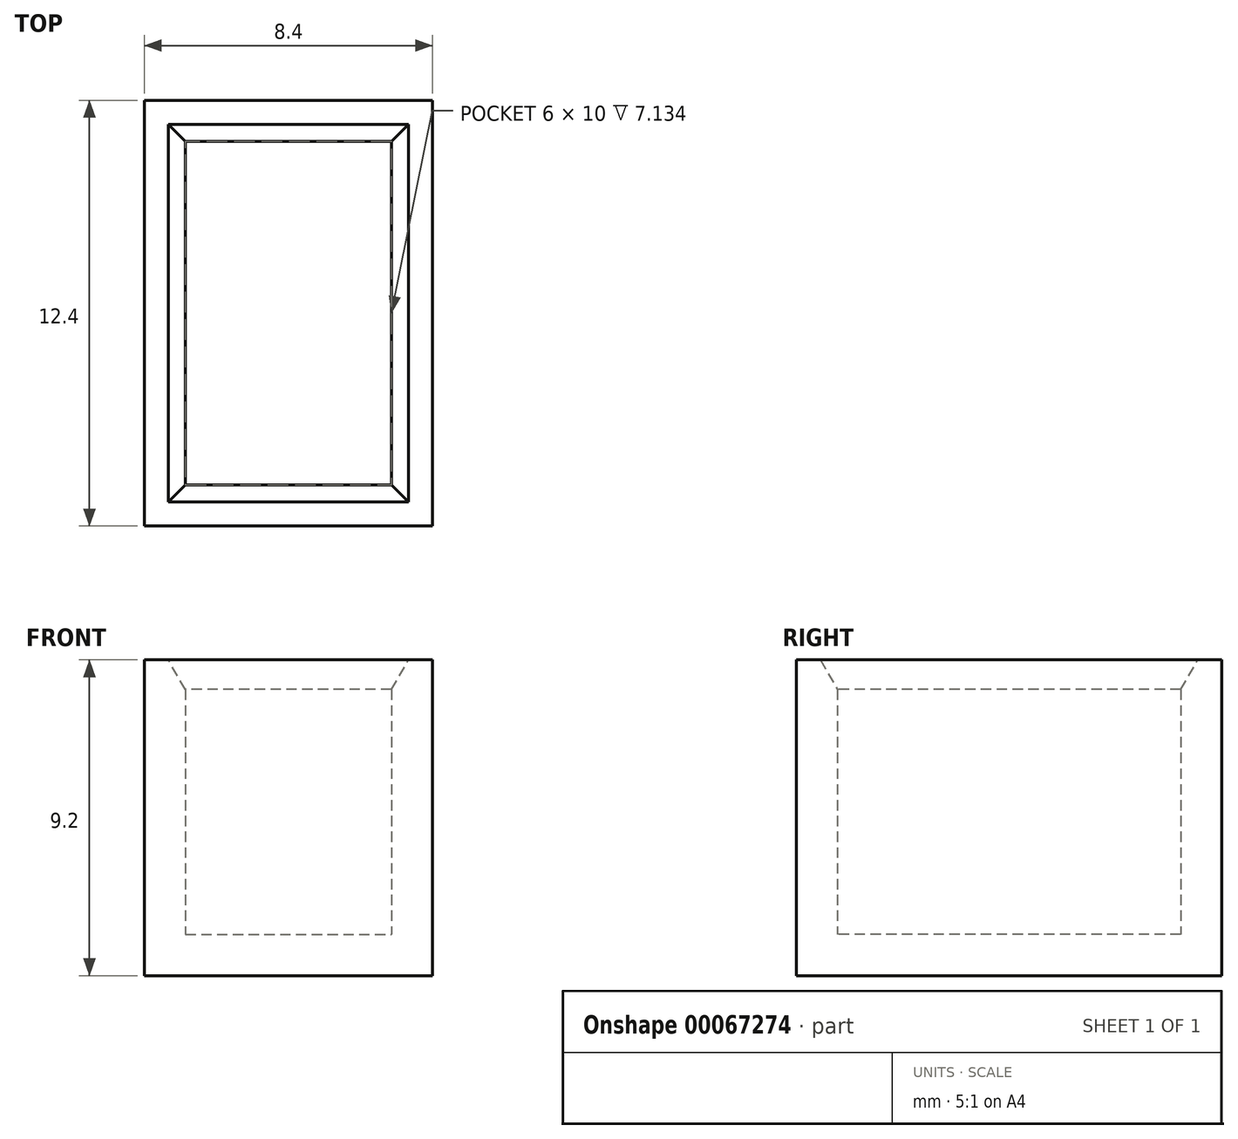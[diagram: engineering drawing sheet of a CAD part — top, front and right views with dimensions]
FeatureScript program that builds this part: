
annotation { "Feature Type Name" : "Feature", "Feature Type Description" : "" }
export const myFeature = defineFeature(function(context is Context, id is Id, definition is map)
    precondition{}
    {
        {
            var Q0;
            Q0=qCreatedBy(makeId("Top.planeOp"),FACE);
            var sketch = newSketch(context, id + "F0", { "sketchPlane" : qUnion([Q0])});
            skLineSegment(sketch, "E0.bottom", {"start": v(-3, 5) * mm, "end": v(3, 5) * mm});
            skLineSegment(sketch, "E0.top", {"start": v(-3, -5) * mm, "end": v(3, -5) * mm});
            skLineSegment(sketch, "E0.left", {"start": v(-3, 5) * mm, "end": v(-3, -5) * mm});
            skLineSegment(sketch, "E0.right", {"start": v(3, 5) * mm, "end": v(3, -5) * mm});
            skPoint(sketch, "E0.middle", {"position": v(0, 0) * mm});
            skSolve(sketch);
        }
        {
            var Q0;
            Q0 = qSketchRegion(id + "F0", true);
            extrude(context, id + "F1", {"entities" : qUnion([Q0]), "depth" : 8 * mm});
        }
        {
            var Q0;
            Q0=makeQuery(id+"F1.opExtrude","CAP_FACE",FACE,{"disambiguationData":[OSD([sQuery(id+"F0.wireOp",EDGE,"E0.bottom"),sQuery(id+"F0.wireOp",EDGE,"E0.top"),sQuery(id+"F0.wireOp",EDGE,"E0.left"),sQuery(id+"F0.wireOp",EDGE,"E0.right")])],"isStart":false});
            shell(context, id + "F2", {"entities" : qUnion([Q0]), "thickness" : 1.2 * mm, "oppositeDirection" : true});
        }
        {
            var Q0;
            {var subQ0=sQuery(id+"F0.wireOp",EDGE,"E0.bottom");Q0=makeQuery(id+"F2.opShell","OFFSET_EDGE",EDGE,{"disambiguationData":[OSD([subQ0]),TDD([makeQuery(id+"F1.opExtrude","CAP_EDGE",EDGE,{"disambiguationData":[OSD([subQ0])],"isStart":false})])]});}
            var Q1;
            {var subQ0=sQuery(id+"F0.wireOp",EDGE,"E0.left");Q1=makeQuery(id+"F2.opShell","OFFSET_EDGE",EDGE,{"disambiguationData":[OSD([subQ0]),TDD([makeQuery(id+"F1.opExtrude","CAP_EDGE",EDGE,{"disambiguationData":[OSD([subQ0])],"isStart":false})])]});}
            var Q2;
            {var subQ0=sQuery(id+"F0.wireOp",EDGE,"E0.right");Q2=makeQuery(id+"F2.opShell","OFFSET_EDGE",EDGE,{"disambiguationData":[OSD([subQ0]),TDD([makeQuery(id+"F1.opExtrude","CAP_EDGE",EDGE,{"disambiguationData":[OSD([subQ0])],"isStart":false})])]});}
            var Q3;
            {var subQ0=sQuery(id+"F0.wireOp",EDGE,"E0.top");Q3=makeQuery(id+"F2.opShell","OFFSET_EDGE",EDGE,{"disambiguationData":[OSD([subQ0]),TDD([makeQuery(id+"F1.opExtrude","CAP_EDGE",EDGE,{"disambiguationData":[OSD([subQ0])],"isStart":false})])]});}
            chamfer(context, id + "F3", {"entities" : qUnion([Q0, Q1, Q2, Q3]), "chamferType" : ChamferType.OFFSET_ANGLE, "width" : 0.5 * mm, "oppositeDirection" : false, "angle" : 60 * degree, "tangentPropagation" : true});
        }
    });
